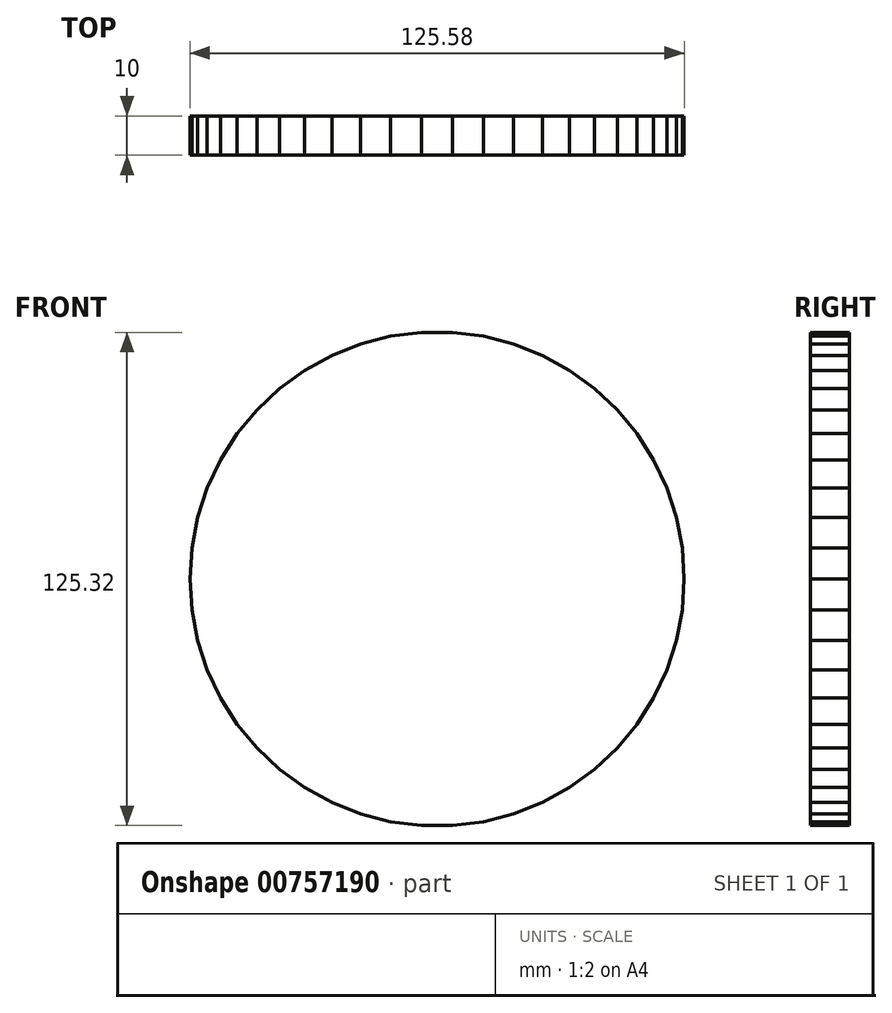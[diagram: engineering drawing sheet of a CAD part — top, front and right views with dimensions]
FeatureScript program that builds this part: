
annotation { "Feature Type Name" : "Feature", "Feature Type Description" : "" }
export const myFeature = defineFeature(function(context is Context, id is Id, definition is map)
    precondition{}
    {
        {
            var Q0;
            Q0=qCreatedBy(makeId("Front.planeOp"),FACE);
            var sketch = newSketch(context, id + "F0", { "sketchPlane" : qUnion([Q0])});
            skCircle(sketch, "E0.cCircle", {"center": v(0, 0) * mm, "radius": 62.66 * mm, "construction": true});
            skLineSegment(sketch, "E0.0", {"start": v(-3.94, 62.66) * mm, "end": v(3.94, 62.66) * mm});
            skLineSegment(sketch, "E0.1", {"start": v(3.94, 62.66) * mm, "end": v(11.76, 61.67) * mm});
            skLineSegment(sketch, "E0.2", {"start": v(11.76, 61.67) * mm, "end": v(19.4, 59.71) * mm});
            skLineSegment(sketch, "E0.3", {"start": v(19.4, 59.71) * mm, "end": v(26.73, 56.8) * mm});
            skLineSegment(sketch, "E0.4", {"start": v(26.73, 56.8) * mm, "end": v(33.64, 53.01) * mm});
            skLineSegment(sketch, "E0.5", {"start": v(33.64, 53.01) * mm, "end": v(40.02, 48.38) * mm});
            skLineSegment(sketch, "E0.6", {"start": v(40.02, 48.38) * mm, "end": v(45.77, 42.98) * mm});
            skLineSegment(sketch, "E0.7", {"start": v(45.77, 42.98) * mm, "end": v(50.8, 36.9) * mm});
            skLineSegment(sketch, "E0.8", {"start": v(50.8, 36.9) * mm, "end": v(55.02, 30.25) * mm});
            skLineSegment(sketch, "E0.9", {"start": v(55.02, 30.25) * mm, "end": v(58.38, 23.11) * mm});
            skLineSegment(sketch, "E0.10", {"start": v(58.38, 23.11) * mm, "end": v(60.81, 15.61) * mm});
            skLineSegment(sketch, "E0.11", {"start": v(60.81, 15.61) * mm, "end": v(62.3, 7.87) * mm});
            skLineSegment(sketch, "E0.12", {"start": v(62.3, 7.87) * mm, "end": v(62.79, 0) * mm});
            skLineSegment(sketch, "E0.13", {"start": v(62.79, 0) * mm, "end": v(62.3, -7.87) * mm});
            skLineSegment(sketch, "E0.14", {"start": v(62.3, -7.87) * mm, "end": v(60.81, -15.61) * mm});
            skLineSegment(sketch, "E0.15", {"start": v(60.81, -15.61) * mm, "end": v(58.38, -23.11) * mm});
            skLineSegment(sketch, "E0.16", {"start": v(58.38, -23.11) * mm, "end": v(55.02, -30.25) * mm});
            skLineSegment(sketch, "E0.17", {"start": v(55.02, -30.25) * mm, "end": v(50.8, -36.9) * mm});
            skLineSegment(sketch, "E0.18", {"start": v(50.8, -36.9) * mm, "end": v(45.77, -42.98) * mm});
            skLineSegment(sketch, "E0.19", {"start": v(45.77, -42.98) * mm, "end": v(40.02, -48.38) * mm});
            skLineSegment(sketch, "E0.20", {"start": v(40.02, -48.38) * mm, "end": v(33.64, -53.01) * mm});
            skLineSegment(sketch, "E0.21", {"start": v(33.64, -53.01) * mm, "end": v(26.73, -56.8) * mm});
            skLineSegment(sketch, "E0.22", {"start": v(26.73, -56.8) * mm, "end": v(19.4, -59.71) * mm});
            skLineSegment(sketch, "E0.23", {"start": v(19.4, -59.71) * mm, "end": v(11.76, -61.67) * mm});
            skLineSegment(sketch, "E0.24", {"start": v(11.76, -61.67) * mm, "end": v(3.94, -62.66) * mm});
            skLineSegment(sketch, "E0.25", {"start": v(3.94, -62.66) * mm, "end": v(-3.94, -62.66) * mm});
            skLineSegment(sketch, "E0.26", {"start": v(-3.94, -62.66) * mm, "end": v(-11.76, -61.67) * mm});
            skLineSegment(sketch, "E0.27", {"start": v(-11.76, -61.67) * mm, "end": v(-19.4, -59.71) * mm});
            skLineSegment(sketch, "E0.28", {"start": v(-19.4, -59.71) * mm, "end": v(-26.73, -56.8) * mm});
            skLineSegment(sketch, "E0.29", {"start": v(-26.73, -56.8) * mm, "end": v(-33.64, -53.01) * mm});
            skLineSegment(sketch, "E0.30", {"start": v(-33.64, -53.01) * mm, "end": v(-40.02, -48.38) * mm});
            skLineSegment(sketch, "E0.31", {"start": v(-40.02, -48.38) * mm, "end": v(-45.77, -42.98) * mm});
            skLineSegment(sketch, "E0.32", {"start": v(-45.77, -42.98) * mm, "end": v(-50.8, -36.9) * mm});
            skLineSegment(sketch, "E0.33", {"start": v(-50.8, -36.9) * mm, "end": v(-55.02, -30.25) * mm});
            skLineSegment(sketch, "E0.34", {"start": v(-55.02, -30.25) * mm, "end": v(-58.38, -23.11) * mm});
            skLineSegment(sketch, "E0.35", {"start": v(-58.38, -23.11) * mm, "end": v(-60.81, -15.61) * mm});
            skLineSegment(sketch, "E0.36", {"start": v(-60.81, -15.61) * mm, "end": v(-62.3, -7.87) * mm});
            skLineSegment(sketch, "E0.37", {"start": v(-62.3, -7.87) * mm, "end": v(-62.79, 0) * mm});
            skLineSegment(sketch, "E0.38", {"start": v(-62.79, 0) * mm, "end": v(-62.3, 7.87) * mm});
            skLineSegment(sketch, "E0.39", {"start": v(-62.3, 7.87) * mm, "end": v(-60.81, 15.61) * mm});
            skLineSegment(sketch, "E0.40", {"start": v(-60.81, 15.61) * mm, "end": v(-58.38, 23.11) * mm});
            skLineSegment(sketch, "E0.41", {"start": v(-58.38, 23.11) * mm, "end": v(-55.02, 30.25) * mm});
            skLineSegment(sketch, "E0.42", {"start": v(-55.02, 30.25) * mm, "end": v(-50.8, 36.9) * mm});
            skLineSegment(sketch, "E0.43", {"start": v(-50.8, 36.9) * mm, "end": v(-45.77, 42.98) * mm});
            skLineSegment(sketch, "E0.44", {"start": v(-45.77, 42.98) * mm, "end": v(-40.02, 48.38) * mm});
            skLineSegment(sketch, "E0.45", {"start": v(-40.02, 48.38) * mm, "end": v(-33.64, 53.01) * mm});
            skLineSegment(sketch, "E0.46", {"start": v(-33.64, 53.01) * mm, "end": v(-26.73, 56.8) * mm});
            skLineSegment(sketch, "E0.47", {"start": v(-26.73, 56.8) * mm, "end": v(-19.4, 59.71) * mm});
            skLineSegment(sketch, "E0.48", {"start": v(-19.4, 59.71) * mm, "end": v(-11.76, 61.67) * mm});
            skLineSegment(sketch, "E0.49", {"start": v(-11.76, 61.67) * mm, "end": v(-3.94, 62.66) * mm});
            skPoint(sketch, "E0.0.midPoint", {"position": v(0, 62.66) * mm});
            skSolve(sketch);
        }
        {
            var Q0;
            Q0=makeQuery(id+"F0.imprint","IMPRINT",FACE,{"disambiguationData":[TD([[makeQuery(id+"F0.imprint","IMPRINT",EDGE,{"derivedFrom":sQuery(id+"F0.wireOp",EDGE,"E0.0")}),-1.0]])]});
            var sketch = newSketch(context, id + "F1", { "sketchPlane" : qUnion([Q0])});
            skLineSegment(sketch, "E1.0", {"start": v(-58.38, 23.11) * mm, "end": v(-55.02, 30.25) * mm});
            skLineSegment(sketch, "E1.1", {"start": v(3.94, -62.66) * mm, "end": v(-3.94, -62.66) * mm});
            skLineSegment(sketch, "E1.2", {"start": v(-55.02, -30.25) * mm, "end": v(-58.38, -23.11) * mm});
            skLineSegment(sketch, "E1.3", {"start": v(62.3, 7.87) * mm, "end": v(62.79, 0) * mm});
            skLineSegment(sketch, "E1.4", {"start": v(62.79, 0) * mm, "end": v(62.3, -7.87) * mm});
            skLineSegment(sketch, "E1.5", {"start": v(62.3, -7.87) * mm, "end": v(60.81, -15.61) * mm});
            skCircle(sketch, "E1.6", {"center": v(0, 0) * mm, "radius": 62.66 * mm});
            skLineSegment(sketch, "E1.7", {"start": v(3.94, 62.66) * mm, "end": v(11.76, 61.67) * mm});
            skLineSegment(sketch, "E1.8", {"start": v(11.76, 61.67) * mm, "end": v(19.4, 59.71) * mm});
            skLineSegment(sketch, "E1.9", {"start": v(19.4, 59.71) * mm, "end": v(26.73, 56.8) * mm});
            skLineSegment(sketch, "E1.10", {"start": v(26.73, 56.8) * mm, "end": v(33.64, 53.01) * mm});
            skLineSegment(sketch, "E1.11", {"start": v(33.64, 53.01) * mm, "end": v(40.02, 48.38) * mm});
            skLineSegment(sketch, "E1.12", {"start": v(40.02, 48.38) * mm, "end": v(45.77, 42.98) * mm});
            skLineSegment(sketch, "E1.13", {"start": v(45.77, 42.98) * mm, "end": v(50.8, 36.9) * mm});
            skLineSegment(sketch, "E1.14", {"start": v(50.8, 36.9) * mm, "end": v(55.02, 30.25) * mm});
            skLineSegment(sketch, "E1.15", {"start": v(55.02, 30.25) * mm, "end": v(58.38, 23.11) * mm});
            skLineSegment(sketch, "E1.16", {"start": v(58.38, 23.11) * mm, "end": v(60.81, 15.61) * mm});
            skLineSegment(sketch, "E1.17", {"start": v(60.81, 15.61) * mm, "end": v(62.3, 7.87) * mm});
            skLineSegment(sketch, "E1.18", {"start": v(-3.94, -62.66) * mm, "end": v(-11.76, -61.67) * mm});
            skLineSegment(sketch, "E1.19", {"start": v(-62.79, 0) * mm, "end": v(-62.3, 7.87) * mm});
            skLineSegment(sketch, "E1.20", {"start": v(26.73, -56.8) * mm, "end": v(19.4, -59.71) * mm});
            skLineSegment(sketch, "E1.21", {"start": v(45.77, -42.98) * mm, "end": v(40.02, -48.38) * mm});
            skLineSegment(sketch, "E1.22", {"start": v(-19.4, -59.71) * mm, "end": v(-26.73, -56.8) * mm});
            skLineSegment(sketch, "E1.23", {"start": v(-58.38, -23.11) * mm, "end": v(-60.81, -15.61) * mm});
            skLineSegment(sketch, "E1.24", {"start": v(60.81, -15.61) * mm, "end": v(58.38, -23.11) * mm});
            skLineSegment(sketch, "E1.25", {"start": v(-26.73, 56.8) * mm, "end": v(-19.4, 59.71) * mm});
            skLineSegment(sketch, "E1.26", {"start": v(-40.02, -48.38) * mm, "end": v(-45.77, -42.98) * mm});
            skLineSegment(sketch, "E1.27", {"start": v(-11.76, -61.67) * mm, "end": v(-19.4, -59.71) * mm});
            skLineSegment(sketch, "E1.28", {"start": v(-62.3, 7.87) * mm, "end": v(-60.81, 15.61) * mm});
            skLineSegment(sketch, "E1.29", {"start": v(19.4, -59.71) * mm, "end": v(11.76, -61.67) * mm});
            skLineSegment(sketch, "E1.30", {"start": v(40.02, -48.38) * mm, "end": v(33.64, -53.01) * mm});
            skLineSegment(sketch, "E1.31", {"start": v(-40.02, 48.38) * mm, "end": v(-33.64, 53.01) * mm});
            skLineSegment(sketch, "E1.32", {"start": v(-26.73, -56.8) * mm, "end": v(-33.64, -53.01) * mm});
            skLineSegment(sketch, "E1.33", {"start": v(-60.81, -15.61) * mm, "end": v(-62.3, -7.87) * mm});
            skLineSegment(sketch, "E1.34", {"start": v(58.38, -23.11) * mm, "end": v(55.02, -30.25) * mm});
            skLineSegment(sketch, "E1.35", {"start": v(-19.4, 59.71) * mm, "end": v(-11.76, 61.67) * mm});
            skLineSegment(sketch, "E1.36", {"start": v(-45.77, -42.98) * mm, "end": v(-50.8, -36.9) * mm});
            skLineSegment(sketch, "E1.37", {"start": v(-60.81, 15.61) * mm, "end": v(-58.38, 23.11) * mm});
            skLineSegment(sketch, "E1.38", {"start": v(11.76, -61.67) * mm, "end": v(3.94, -62.66) * mm});
            skLineSegment(sketch, "E1.39", {"start": v(33.64, -53.01) * mm, "end": v(26.73, -56.8) * mm});
            skLineSegment(sketch, "E1.40", {"start": v(-33.64, 53.01) * mm, "end": v(-26.73, 56.8) * mm});
            skLineSegment(sketch, "E1.41", {"start": v(-33.64, -53.01) * mm, "end": v(-40.02, -48.38) * mm});
            skLineSegment(sketch, "E1.42", {"start": v(-62.3, -7.87) * mm, "end": v(-62.79, 0) * mm});
            skLineSegment(sketch, "E1.43", {"start": v(-11.76, 61.67) * mm, "end": v(-3.94, 62.66) * mm});
            skLineSegment(sketch, "E1.44", {"start": v(-50.8, -36.9) * mm, "end": v(-55.02, -30.25) * mm});
            skLineSegment(sketch, "E2", {"start": v(-3.94, 62.66) * mm, "end": v(-19.4, -59.71) * mm});
            skLineSegment(sketch, "E3", {"start": v(-19.4, -59.71) * mm, "end": v(40.02, 48.38) * mm});
            skLineSegment(sketch, "E4", {"start": v(40.02, 48.38) * mm, "end": v(-55.02, -30.25) * mm});
            skLineSegment(sketch, "E5", {"start": v(-55.02, -30.25) * mm, "end": v(62.3, 7.87) * mm});
            skLineSegment(sketch, "E6", {"start": v(62.3, 7.87) * mm, "end": v(-60.81, 15.61) * mm});
            skLineSegment(sketch, "E7", {"start": v(-60.81, 15.61) * mm, "end": v(50.64, -36.9) * mm});
            skLineSegment(sketch, "E8", {"start": v(50.64, -36.9) * mm, "end": v(-33.64, 53.01) * mm});
            skLineSegment(sketch, "E9", {"start": v(-33.64, 53.01) * mm, "end": v(11.76, -61.67) * mm});
            skLineSegment(sketch, "E10", {"start": v(11.76, -61.67) * mm, "end": v(11.76, 61.67) * mm});
            skLineSegment(sketch, "E11", {"start": v(11.76, 61.67) * mm, "end": v(-33.64, -53.01) * mm});
            skLineSegment(sketch, "E12", {"start": v(-33.64, -53.01) * mm, "end": v(50.8, 36.9) * mm});
            skLineSegment(sketch, "E13", {"start": v(50.8, 36.9) * mm, "end": v(-60.81, -15.61) * mm});
            skLineSegment(sketch, "E14", {"start": v(-60.81, -15.61) * mm, "end": v(62.3, -7.87) * mm});
            skLineSegment(sketch, "E15", {"start": v(62.3, -7.87) * mm, "end": v(-55.02, 30.25) * mm});
            skLineSegment(sketch, "E16", {"start": v(-55.02, 30.25) * mm, "end": v(40.02, -48.38) * mm});
            skLineSegment(sketch, "E17", {"start": v(40.02, -48.38) * mm, "end": v(-19.4, 59.71) * mm});
            skLineSegment(sketch, "E18", {"start": v(-19.4, 59.71) * mm, "end": v(-3.94, -62.66) * mm});
            skLineSegment(sketch, "E19", {"start": v(-3.94, -62.66) * mm, "end": v(26.73, 56.8) * mm});
            skLineSegment(sketch, "E20", {"start": v(26.73, 56.8) * mm, "end": v(-45.77, -42.98) * mm});
            skLineSegment(sketch, "E21", {"start": v(-45.77, -42.98) * mm, "end": v(58.38, 23.11) * mm});
            skLineSegment(sketch, "E22", {"start": v(58.38, 23.11) * mm, "end": v(-62.79, 0) * mm});
            skLineSegment(sketch, "E23", {"start": v(-62.79, 0) * mm, "end": v(58.38, -23.11) * mm});
            skLineSegment(sketch, "E24", {"start": v(58.38, -23.11) * mm, "end": v(-45.6, 42.98) * mm});
            skLineSegment(sketch, "E25", {"start": v(-45.6, 42.98) * mm, "end": v(26.73, -56.8) * mm});
            skLineSegment(sketch, "E26", {"start": v(26.73, -56.8) * mm, "end": v(-3.94, 62.66) * mm});
            skSolve(sketch);
        }
        {
            var Q0;
            Q0 = qSketchRegion(id + "F0", true);
            extrude(context, id + "F2", {"entities" : qUnion([Q0]), "depth" : 10 * mm, "offsetDistance" : 25 * mm});
        }
    });
